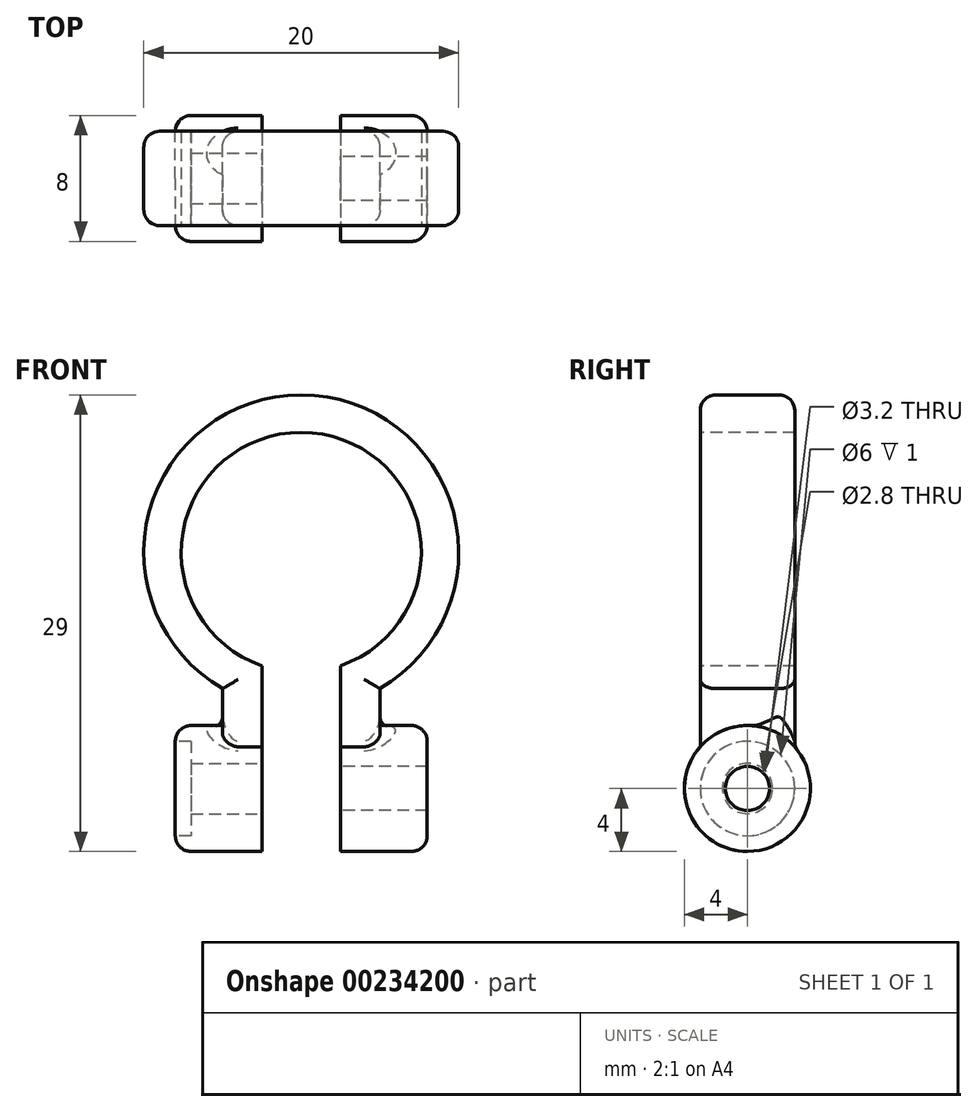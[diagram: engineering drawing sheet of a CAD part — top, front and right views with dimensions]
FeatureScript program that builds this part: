
annotation { "Feature Type Name" : "Feature", "Feature Type Description" : "" }
export const myFeature = defineFeature(function(context is Context, id is Id, definition is map)
    precondition{}
    {
        {
            var Q0;
            Q0=qCreatedBy(makeId("Front.planeOp"),FACE);
            var sketch = newSketch(context, id + "F0", { "sketchPlane" : qUnion([Q0])});
            skCircle(sketch, "E0", {"center": v(0, 0) * mm, "radius": 10 * mm});
            skSolve(sketch);
        }
        {
            var Q0;
            Q0=qSketchRegion(id+"F0",true);
            extrude(context, id + "F1", {"entities" : qUnion([Q0]), "depth" : 5 * mm, "hasSecondDirection" : true, "secondDirectionOppositeDirection" : true, "secondDirectionDepth" : 1 * mm});
        }
        {
            var Q0;
            Q0=makeQuery(id+"F1.opExtrude","CAP_FACE",FACE,{"disambiguationData":[OSD([sQuery(id+"F0.wireOp",EDGE,"E0")])],"isStart":false});
            var sketch = newSketch(context, id + "F2", { "sketchPlane" : qUnion([Q0])});
            skCircle(sketch, "E1", {"center": v(0, 0) * mm, "radius": 7.62 * mm});
            skSolve(sketch);
        }
        {
            var Q0;
            Q0=qSketchRegion(id+"F2",true);
            extrude(context, id + "F3", {"entities" : qUnion([Q0]), "operationType" : NewBodyOperationType.REMOVE, "endBound" : BoundingType.THROUGH_ALL, "oppositeDirection" : true, "depth" : 25 * mm});
        }
        {
            var Q0;
            Q0=qCreatedBy(makeId("Right.planeOp"),FACE);
            var sketch = newSketch(context, id + "F4", { "sketchPlane" : qUnion([Q0])});
            skLineSegment(sketch, "E2.0", {"start": v(1, -10) * mm, "end": v(1, 10) * mm, "construction": true});
            skLineSegment(sketch, "E3.0", {"start": v(-5, -10) * mm, "end": v(-5, 10) * mm, "construction": true});
            skLineSegment(sketch, "E4", {"start": v(-5, -10) * mm, "end": v(1, -10) * mm, "construction": true});
            skLineSegment(sketch, "E5", {"start": v(-2, -10) * mm, "end": v(-2, -15) * mm, "construction": true});
            skCircle(sketch, "E6", {"center": v(-2, -15) * mm, "radius": 4 * mm});
            skSolve(sketch);
        }
        {
            var Q0;
            Q0=qSketchRegion(id+"F4",true);
            extrude(context, id + "F5", {"entities" : qUnion([Q0]), "depth" : 8 * mm, "hasSecondDirection" : true, "secondDirectionOppositeDirection" : true, "secondDirectionDepth" : 8 * mm});
        }
        {
            var Q0;
            Q0=qCreatedBy(makeId("Front.planeOp"),FACE);
            var sketch = newSketch(context, id + "F6", { "sketchPlane" : qUnion([Q0])});
            skLineSegment(sketch, "E7", {"start": v(0, 0) * mm, "end": v(0, -7.62) * mm, "construction": true});
            skLineSegment(sketch, "E8.bottom", {"start": v(-5, -7.62) * mm, "end": v(5, -7.63) * mm});
            skLineSegment(sketch, "E8.top", {"start": v(-5, -15) * mm, "end": v(5, -15) * mm});
            skLineSegment(sketch, "E8.left", {"start": v(-5, -7.63) * mm, "end": v(-5, -15) * mm});
            skLineSegment(sketch, "E8.right", {"start": v(5, -7.62) * mm, "end": v(5, -15) * mm});
            skLineSegment(sketch, "E9.0", {"start": v(-8, -11) * mm, "end": v(-8, -19) * mm, "construction": true});
            skLineSegment(sketch, "E10", {"start": v(-8, -15) * mm, "end": v(-5, -15) * mm, "construction": true});
            skSolve(sketch);
        }
        {
            var Q0;
            Q0=qSketchRegion(id+"F6",true);
            extrude(context, id + "F7", {"entities" : qUnion([Q0]), "operationType" : NewBodyOperationType.ADD, "depth" : 5 * mm, "hasSecondDirection" : true, "secondDirectionOppositeDirection" : true, "secondDirectionDepth" : 1 * mm});
        }
        {
            var Q0;
            Q0=qCreatedBy(makeId("Front.planeOp"),FACE);
            var sketch = newSketch(context, id + "F8", { "sketchPlane" : qUnion([Q0])});
            skLineSegment(sketch, "E11.bottom", {"start": v(-2.5, 0) * mm, "end": v(2.5, 0) * mm});
            skLineSegment(sketch, "E11.top", {"start": v(-2.5, -25.02) * mm, "end": v(2.5, -25.02) * mm});
            skLineSegment(sketch, "E11.left", {"start": v(-2.5, 0) * mm, "end": v(-2.5, -25.02) * mm});
            skLineSegment(sketch, "E11.right", {"start": v(2.5, 0) * mm, "end": v(2.5, -25.02) * mm});
            skSolve(sketch);
        }
        {
            var Q0;
            Q0=qSketchRegion(id+"F8",true);
            extrude(context, id + "F9", {"entities" : qUnion([Q0]), "operationType" : NewBodyOperationType.REMOVE, "endBound" : BoundingType.THROUGH_ALL, "oppositeDirection" : true, "depth" : 25 * mm, "hasSecondDirection" : true, "secondDirectionBound" : SecondDirectionBoundingType.THROUGH_ALL, "secondDirectionOppositeDirection" : false, "secondDirectionDepth" : 25 * mm});
        }
        {
            var Q0;
            Q0=qCreatedBy(makeId("Right.planeOp"),FACE);
            var sketch = newSketch(context, id + "F10", { "sketchPlane" : qUnion([Q0])});
            skCircle(sketch, "E12.0", {"center": v(-2, -15) * mm, "radius": 4 * mm, "construction": true});
            skCircle(sketch, "E13", {"center": v(-2, -15) * mm, "radius": 1.6 * mm});
            skSolve(sketch);
        }
        {
            var Q0;
            Q0=qSketchRegion(id+"F10",true);
            extrude(context, id + "F11", {"entities" : qUnion([Q0]), "operationType" : NewBodyOperationType.REMOVE, "endBound" : BoundingType.THROUGH_ALL, "oppositeDirection" : true, "depth" : 25 * mm});
        }
        {
            var Q0;
            Q0=makeQuery(id+"F5.opExtrude","CAP_FACE",FACE,{"disambiguationData":[OSD([sQuery(id+"F4.wireOp",EDGE,"E6")])],"isStart":true});
            var sketch = newSketch(context, id + "F12", { "sketchPlane" : qUnion([Q0])});
            skCircle(sketch, "E14", {"center": v(2, -15) * mm, "radius": 3 * mm});
            skSolve(sketch);
        }
        {
            var Q0;
            Q0=qSketchRegion(id+"F12",true);
            extrude(context, id + "F13", {"entities" : qUnion([Q0]), "operationType" : NewBodyOperationType.REMOVE, "oppositeDirection" : true, "depth" : 1 * mm});
        }
        {
            var Q0;
            Q0=qCreatedBy(makeId("Right.planeOp"),FACE);
            var sketch = newSketch(context, id + "F14", { "sketchPlane" : qUnion([Q0])});
            skCircle(sketch, "E15.0", {"center": v(-2, -15) * mm, "radius": 4 * mm, "construction": true});
            skCircle(sketch, "E16", {"center": v(-2, -15) * mm, "radius": 1.4 * mm});
            skSolve(sketch);
        }
        {
            var Q0;
            Q0=qSketchRegion(id+"F14",true);
            extrude(context, id + "F15", {"entities" : qUnion([Q0]), "operationType" : NewBodyOperationType.REMOVE, "endBound" : BoundingType.THROUGH_ALL, "depth" : 25 * mm});
        }
        {
            var Q0;
            {var subQ0=sQuery(id+"F6.wireOp",EDGE,"E8.right");var subQ1=sQuery(id+"F0.wireOp",EDGE,"E0");Q0=makeQuery(id+"Fy1vDWqXbtszQ1z_1.boolean.opBoolean","SPLIT",EDGE,{"disambiguationData":[TD([makeQuery(id+"F7.opExtrude","SWEPT_FACE",FACE,{"disambiguationData":[OSD([subQ0])]})])],"derivedFrom":makeQuery(id+"F1.opExtrude","CAP_EDGE",EDGE,{"disambiguationData":[OSD([subQ1])],"isStart":false})});}
            var Q1;
            Q1=makeQuery(id+"Fy1vDWqXbtszQ1z_1.opExtrude","CAP_EDGE",EDGE,{"disambiguationData":[OSD([sQuery(id+"FDFqeWie7hZFsKc_1.wireOp",EDGE,"6763f5b2-1f24-450c-af15-a88bf6d05757.2")])],"isStart":true});
            var Q2;
            Q2=makeQuery(id+"Fy1vDWqXbtszQ1z_1.opExtrude","CAP_EDGE",EDGE,{"disambiguationData":[OSD([sQuery(id+"FDFqeWie7hZFsKc_1.wireOp",EDGE,"6763f5b2-1f24-450c-af15-a88bf6d05757.1")])],"isStart":true});
            var Q3;
            Q3=makeQuery(id+"Fy1vDWqXbtszQ1z_1.opExtrude","CAP_EDGE",EDGE,{"disambiguationData":[OSD([sQuery(id+"FDFqeWie7hZFsKc_1.wireOp",EDGE,"6763f5b2-1f24-450c-af15-a88bf6d05757.0")])],"isStart":true});
            var Q4;
            {var subQ0=sQuery(id+"F6.wireOp",EDGE,"E8.left");var subQ1=sQuery(id+"F0.wireOp",EDGE,"E0");Q4=makeQuery(id+"Fy1vDWqXbtszQ1z_1.boolean.opBoolean","SPLIT",EDGE,{"disambiguationData":[TD([makeQuery(id+"F7.opExtrude","SWEPT_FACE",FACE,{"disambiguationData":[OSD([subQ0])]})])],"derivedFrom":makeQuery(id+"F1.opExtrude","CAP_EDGE",EDGE,{"disambiguationData":[OSD([subQ1])],"isStart":false})});}
            var Q5;
            Q5=makeQuery(id+"F7.opExtrude","CAP_EDGE",EDGE,{"disambiguationData":[OSD([sQuery(id+"F6.wireOp",EDGE,"E8.left")])],"isStart":false});
            var Q6;
            Q6=makeQuery(id+"F7.opExtrude","CAP_EDGE",EDGE,{"disambiguationData":[OSD([sQuery(id+"F6.wireOp",EDGE,"E8.right")])],"isStart":false});
            var Q7;
            {var subQ0=sQuery(id+"F6.wireOp",EDGE,"E8.right");var subQ4=sQuery(id+"F0.wireOp",EDGE,"E0");Q7=makeQuery(id+"Fy1vDWqXbtszQ1z_1.boolean.opBoolean","SPLIT",EDGE,{"disambiguationData":[TD([makeQuery(id+"F7.opExtrude","SWEPT_FACE",FACE,{"disambiguationData":[OSD([subQ0])]})])],"derivedFrom":makeQuery(id+"F1.opExtrude","CAP_EDGE",EDGE,{"disambiguationData":[OSD([subQ4])],"isStart":true})});}
            var Q8;
            {var subQ0=sQuery(id+"FDFqeWie7hZFsKc_1.wireOp",EDGE,"6763f5b2-1f24-450c-af15-a88bf6d05757.2");var subQ2=sQuery(id+"F6.wireOp",EDGE,"E8.right");var subQ3=sQuery(id+"F6.wireOp",EDGE,"E8.left");var subQ4=sQuery(id+"F6.wireOp",EDGE,"E8.top");var subQ5=sQuery(id+"F6.wireOp",EDGE,"E8.bottom");var subQ6=sQuery(id+"F0.wireOp",EDGE,"E0");var subQ7=makeQuery(id+"FDFqeWie7hZFsKc_1.imprint","INTERSECT",VERTEX,{"derivedFrom":[makeQuery(id+"F1.opExtrude","CAP_EDGE",EDGE,{"disambiguationData":[OSD([subQ6])],"isStart":false}),subQ0]});Q8=makeQuery(id+"Fy1vDWqXbtszQ1z_1.opExtrude","TWEAK_EDGE",EDGE,{"derivedFrom":[makeQuery(id+"F7.boolean.opBoolean","MERGE",FACE,{"derivedFrom":[makeQuery(id+"F1.opExtrude","CAP_FACE",FACE,{"disambiguationData":[OSD([subQ6])],"isStart":true}),makeQuery(id+"F7.opExtrude","CAP_FACE",FACE,{"disambiguationData":[OSD([subQ5,subQ4,subQ3,subQ2])],"isStart":true})]}),makeQuery(id+"FDFqeWie7hZFsKc_1.imprint","IMPRINT",EDGE,{"disambiguationData":[TD([[makeQuery(id+"FDFqeWie7hZFsKc_1.imprint","INTERSECT",VERTEX,{"derivedFrom":[sQuery(id+"FDFqeWie7hZFsKc_1.wireOp",EDGE,"6763f5b2-1f24-450c-af15-a88bf6d05757.1"),subQ0]}),-1.0]])],"derivedFrom":subQ0}),makeQuery(id+"FDFqeWie7hZFsKc_1.imprint","IMPRINT",EDGE,{"disambiguationData":[TD([[subQ7,-1.0]])],"derivedFrom":subQ0})]});}
            var Q9;
            Q9=makeQuery(id+"Fy1vDWqXbtszQ1z_1.opExtrude","TWEAK_EDGE",EDGE,{"derivedFrom":[makeQuery(id+"F7.boolean.opBoolean","MERGE",FACE,{"derivedFrom":[makeQuery(id+"F1.opExtrude","CAP_FACE",FACE,{"disambiguationData":[OSD([sQuery(id+"F0.wireOp",EDGE,"E0")])],"isStart":true}),makeQuery(id+"F7.opExtrude","CAP_FACE",FACE,{"disambiguationData":[OSD([sQuery(id+"F6.wireOp",EDGE,"E8.bottom"),sQuery(id+"F6.wireOp",EDGE,"E8.top"),sQuery(id+"F6.wireOp",EDGE,"E8.left"),sQuery(id+"F6.wireOp",EDGE,"E8.right")])],"isStart":true})]}),makeQuery(id+"FDFqeWie7hZFsKc_1.imprint","IMPRINT",EDGE,{"derivedFrom":sQuery(id+"FDFqeWie7hZFsKc_1.wireOp",EDGE,"6763f5b2-1f24-450c-af15-a88bf6d05757.1")})]});
            var Q10;
            {var subQ0=sQuery(id+"FDFqeWie7hZFsKc_1.wireOp",EDGE,"6763f5b2-1f24-450c-af15-a88bf6d05757.0");var subQ2=sQuery(id+"F6.wireOp",EDGE,"E8.right");var subQ3=sQuery(id+"F6.wireOp",EDGE,"E8.left");var subQ4=sQuery(id+"F6.wireOp",EDGE,"E8.top");var subQ5=sQuery(id+"F6.wireOp",EDGE,"E8.bottom");var subQ6=sQuery(id+"F0.wireOp",EDGE,"E0");var subQ7=makeQuery(id+"FDFqeWie7hZFsKc_1.imprint","INTERSECT",VERTEX,{"derivedFrom":[makeQuery(id+"F1.opExtrude","CAP_EDGE",EDGE,{"disambiguationData":[OSD([subQ6])],"isStart":false}),subQ0]});Q10=makeQuery(id+"Fy1vDWqXbtszQ1z_1.opExtrude","TWEAK_EDGE",EDGE,{"derivedFrom":[makeQuery(id+"F7.boolean.opBoolean","MERGE",FACE,{"derivedFrom":[makeQuery(id+"F1.opExtrude","CAP_FACE",FACE,{"disambiguationData":[OSD([subQ6])],"isStart":true}),makeQuery(id+"F7.opExtrude","CAP_FACE",FACE,{"disambiguationData":[OSD([subQ5,subQ4,subQ3,subQ2])],"isStart":true})]}),makeQuery(id+"FDFqeWie7hZFsKc_1.imprint","IMPRINT",EDGE,{"disambiguationData":[TD([[makeQuery(id+"FDFqeWie7hZFsKc_1.imprint","INTERSECT",VERTEX,{"derivedFrom":[subQ0,sQuery(id+"FDFqeWie7hZFsKc_1.wireOp",EDGE,"6763f5b2-1f24-450c-af15-a88bf6d05757.1")]}),-1.0]])],"derivedFrom":subQ0}),makeQuery(id+"FDFqeWie7hZFsKc_1.imprint","IMPRINT",EDGE,{"disambiguationData":[TD([[subQ7,-1.0]])],"derivedFrom":subQ0})]});}
            var Q11;
            {var subQ0=sQuery(id+"F6.wireOp",EDGE,"E8.left");var subQ4=sQuery(id+"F0.wireOp",EDGE,"E0");Q11=makeQuery(id+"Fy1vDWqXbtszQ1z_1.boolean.opBoolean","SPLIT",EDGE,{"disambiguationData":[TD([makeQuery(id+"F7.opExtrude","SWEPT_FACE",FACE,{"disambiguationData":[OSD([subQ0])]})])],"derivedFrom":makeQuery(id+"F1.opExtrude","CAP_EDGE",EDGE,{"disambiguationData":[OSD([subQ4])],"isStart":true})});}
            var Q12;
            Q12=makeQuery(id+"F7.opExtrude","CAP_EDGE",EDGE,{"disambiguationData":[OSD([sQuery(id+"F6.wireOp",EDGE,"E8.left")])],"isStart":true});
            var Q13;
            Q13=makeQuery(id+"F7.opExtrude","CAP_EDGE",EDGE,{"disambiguationData":[OSD([sQuery(id+"F6.wireOp",EDGE,"E8.right")])],"isStart":true});
            var Q14;
            {var subQ0=sQuery(id+"F6.wireOp",EDGE,"E8.right");var subQ1=makeQuery(id+"F7.opExtrude","CAP_FACE",FACE,{"disambiguationData":[OSD([sQuery(id+"F6.wireOp",EDGE,"E8.bottom"),sQuery(id+"F6.wireOp",EDGE,"E8.top"),sQuery(id+"F6.wireOp",EDGE,"E8.left"),subQ0])],"isStart":true});var subQ2=makeQuery(id+"F5.opExtrude","SWEPT_FACE",FACE,{"disambiguationData":[OSD([sQuery(id+"F4.wireOp",EDGE,"E6")])]});Q14=makeQuery(id+"F9.boolean.opBoolean","SPLIT",EDGE,{"disambiguationData":[TD([makeQuery(id+"F7.opExtrude","SWEPT_FACE",FACE,{"disambiguationData":[OSD([subQ0])]})])],"derivedFrom":makeQuery(id+"F7.boolean.opBoolean","INTERSECT",EDGE,{"derivedFrom":[subQ2,subQ1]})});}
            var Q15;
            {var subQ0=sQuery(id+"F6.wireOp",EDGE,"E8.left");var subQ1=makeQuery(id+"F7.opExtrude","CAP_FACE",FACE,{"disambiguationData":[OSD([sQuery(id+"F6.wireOp",EDGE,"E8.bottom"),sQuery(id+"F6.wireOp",EDGE,"E8.top"),subQ0,sQuery(id+"F6.wireOp",EDGE,"E8.right")])],"isStart":true});var subQ2=makeQuery(id+"F5.opExtrude","SWEPT_FACE",FACE,{"disambiguationData":[OSD([sQuery(id+"F4.wireOp",EDGE,"E6")])]});Q15=makeQuery(id+"F9.boolean.opBoolean","SPLIT",EDGE,{"disambiguationData":[TD([makeQuery(id+"F7.opExtrude","SWEPT_FACE",FACE,{"disambiguationData":[OSD([subQ0])]})])],"derivedFrom":makeQuery(id+"F7.boolean.opBoolean","INTERSECT",EDGE,{"derivedFrom":[subQ2,subQ1]})});}
            var Q16;
            Q16=makeQuery(id+"Fy1vDWqXbtszQ1z_1.opExtrude","SWEPT_EDGE",EDGE,{"disambiguationData":[OSD([sQuery(id+"FDFqeWie7hZFsKc_1.wireOp",EDGE,"6763f5b2-1f24-450c-af15-a88bf6d05757.0"),sQuery(id+"FDFqeWie7hZFsKc_1.wireOp",EDGE,"6763f5b2-1f24-450c-af15-a88bf6d05757.1")])]});
            var Q17;
            Q17=makeQuery(id+"Fy1vDWqXbtszQ1z_1.opExtrude","SWEPT_EDGE",EDGE,{"disambiguationData":[OSD([sQuery(id+"FDFqeWie7hZFsKc_1.wireOp",EDGE,"6763f5b2-1f24-450c-af15-a88bf6d05757.1"),sQuery(id+"FDFqeWie7hZFsKc_1.wireOp",EDGE,"6763f5b2-1f24-450c-af15-a88bf6d05757.2")])]});
            var Q18;
            Q18=makeQuery(id+"F5.opExtrude","CAP_EDGE",EDGE,{"disambiguationData":[OSD([sQuery(id+"F4.wireOp",EDGE,"E6")])],"isStart":true});
            var Q19;
            Q19=makeQuery(id+"F5.opExtrude","CAP_EDGE",EDGE,{"disambiguationData":[OSD([sQuery(id+"F4.wireOp",EDGE,"E6")])],"isStart":false});
            fillet(context, id + "F16", {"entities" : qUnion([Q0, Q1, Q2, Q3, Q4, Q5, Q6, Q7, Q8, Q9, Q10, Q11, Q12, Q13, Q14, Q15, Q16, Q17, Q18, Q19]), "radius" : 1 * mm, "tangentPropagation" : true, "allowEdgeOverflow" : false});
        }
    });
